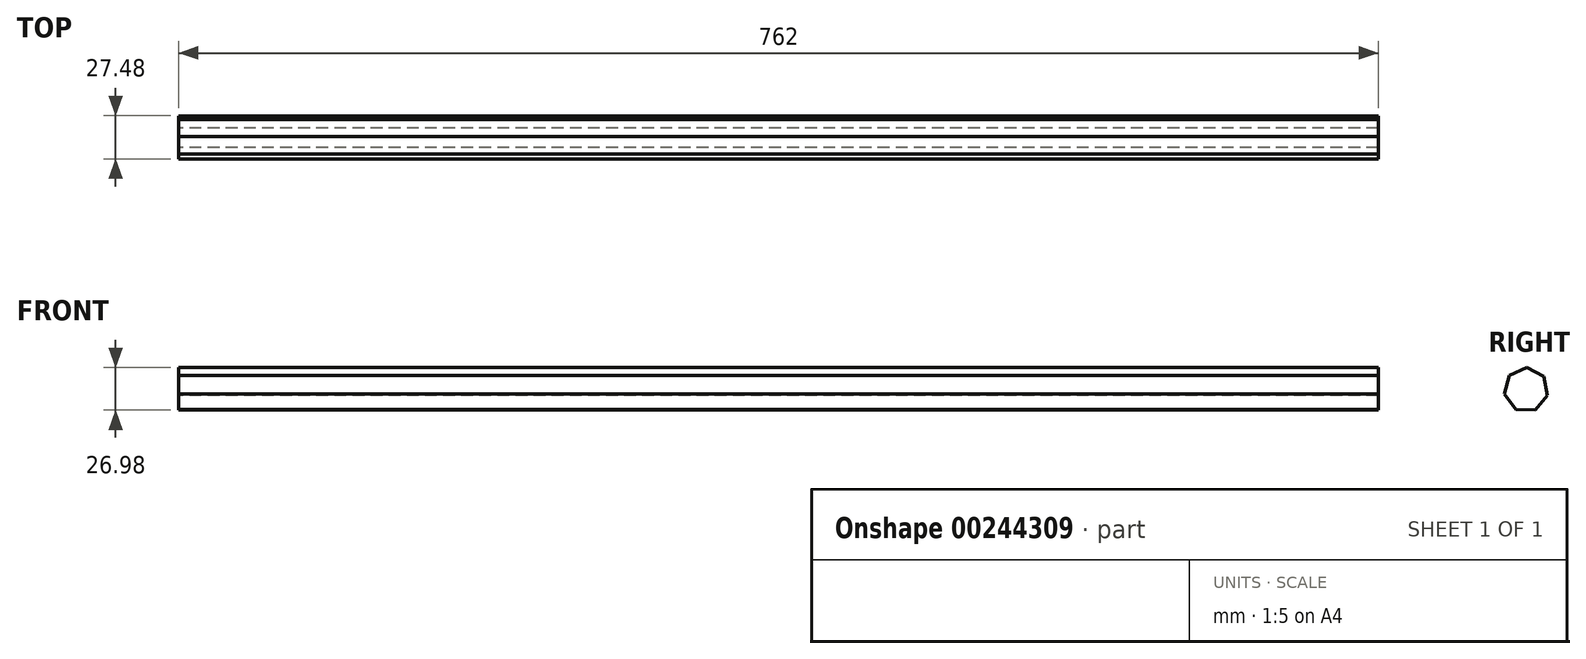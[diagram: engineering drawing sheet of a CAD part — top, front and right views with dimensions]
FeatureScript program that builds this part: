
annotation { "Feature Type Name" : "Feature", "Feature Type Description" : "" }
export const myFeature = defineFeature(function(context is Context, id is Id, definition is map)
    precondition{}
    {
        {
            var Q0;
            Q0=qCreatedBy(makeId("Right.planeOp"),FACE);
            var sketch = newSketch(context, id + "F0", { "sketchPlane" : qUnion([Q0])});
            skCircle(sketch, "E0", {"center": v(0, 0) * mm, "radius": 12.7 * mm});
            skCircle(sketch, "E1.cCircle", {"center": v(0, 0) * mm, "radius": 12.7 * mm, "construction": true});
            skLineSegment(sketch, "E1.0", {"start": v(13.64, -3.57) * mm, "end": v(5.7, -12.89) * mm});
            skLineSegment(sketch, "E1.1", {"start": v(5.7, -12.89) * mm, "end": v(-6.52, -12.5) * mm});
            skLineSegment(sketch, "E1.2", {"start": v(-6.52, -12.5) * mm, "end": v(-13.84, -2.7) * mm});
            skLineSegment(sketch, "E1.3", {"start": v(-13.84, -2.7) * mm, "end": v(-10.74, 9.14) * mm});
            skLineSegment(sketch, "E1.4", {"start": v(-10.74, 9.14) * mm, "end": v(0.45, 14.09) * mm});
            skLineSegment(sketch, "E1.5", {"start": v(0.45, 14.09) * mm, "end": v(11.3, 8.43) * mm});
            skLineSegment(sketch, "E1.6", {"start": v(11.3, 8.43) * mm, "end": v(13.64, -3.57) * mm});
            skPoint(sketch, "E1.0.midPoint", {"position": v(9.67, -8.23) * mm});
            skSolve(sketch);
        }
        {
            var Q0;
            Q0 = qSketchRegion(id + "F0", true);
            extrude(context, id + "F1", {"entities" : qUnion([Q0]), "depth" : 762 * mm});
        }
    });
